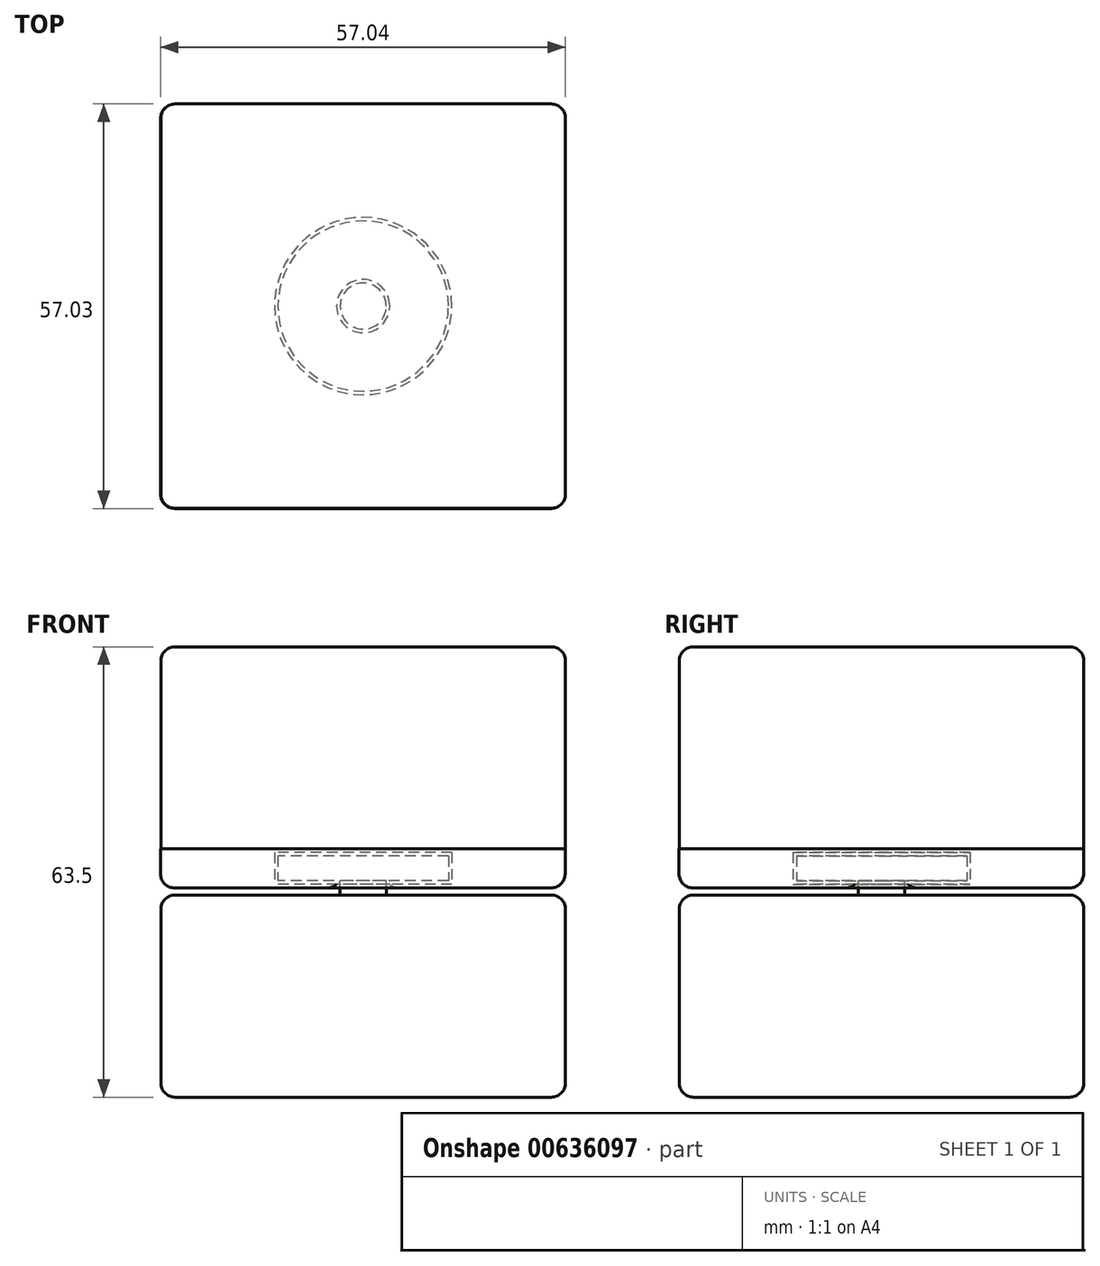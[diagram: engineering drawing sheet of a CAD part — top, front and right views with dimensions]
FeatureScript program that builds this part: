
annotation { "Feature Type Name" : "Feature", "Feature Type Description" : "" }
export const myFeature = defineFeature(function(context is Context, id is Id, definition is map)
    precondition{}
    {
        {
            var Q0;
            Q0=qCreatedBy(makeId("Top.planeOp"),FACE);
            var sketch = newSketch(context, id + "F0", { "sketchPlane" : qUnion([Q0])});
            skCircle(sketch, "E0", {"center": v(0, 0) * mm, "radius": 12.5 * mm});
            skCircle(sketch, "E1", {"center": v(0, 0) * mm, "radius": 13.5 * mm});
            skSolve(sketch);
        }
        {
            var Q0;
            Q0=makeQuery(id+"F0.imprint","IMPRINT",FACE,{"disambiguationData":[TD([[makeQuery(id+"F0.imprint","IMPRINT",EDGE,{"derivedFrom":sQuery(id+"F0.wireOp",EDGE,"E0")}),-1.0]])]});
            extrude(context, id + "F1", {"entities" : qUnion([Q0]), "depth" : 5 * mm, "offsetDistance" : 25 * mm});
        }
        {
            var Q0;
            Q0=qCreatedBy(makeId("Top.planeOp"),FACE);
            cPlane(context, id + "F2", {"entities" : qUnion([Q0]), "cplaneType" : CPlaneType.OFFSET, "offset" : 1 * mm, "width" : 150 * mm, "height" : 150 * mm});
        }
        {
            var Q0;
            Q0=qCreatedBy(id+"F2.planeOp",FACE);
            var sketch = newSketch(context, id + "F3", { "sketchPlane" : qUnion([Q0])});
            skCircle(sketch, "E2", {"center": v(0, 0) * mm, "radius": 12 * mm});
            skSolve(sketch);
        }
        {
            var Q0;
            Q0=makeQuery(id+"F3.imprint","IMPRINT",FACE,{"disambiguationData":[TD([[makeQuery(id+"F3.imprint","IMPRINT",EDGE,{"derivedFrom":sQuery(id+"F3.wireOp",EDGE,"E2")}),1.0]])]});
            extrude(context, id + "F4", {"entities" : qUnion([Q0]), "depth" : 3.5 * mm, "offsetDistance" : 25 * mm});
        }
        {
            var Q0;
            Q0=qCreatedBy(makeId("Top.planeOp"),FACE);
            var sketch = newSketch(context, id + "F5", { "sketchPlane" : qUnion([Q0])});
            skCircle(sketch, "E3", {"center": v(0, 0) * mm, "radius": 12.5 * mm});
            skCircle(sketch, "E4", {"center": v(0, 0) * mm, "radius": 3.75 * mm});
            skSolve(sketch);
        }
        {
            var Q0;
            Q0=makeQuery(id+"F5.imprint","IMPRINT",FACE,{"disambiguationData":[TD([[makeQuery(id+"F5.imprint","IMPRINT",EDGE,{"derivedFrom":sQuery(id+"F5.wireOp",EDGE,"E3")}),1.0]])]});
            extrude(context, id + "F6", {"entities" : qUnion([Q0]), "operationType" : NewBodyOperationType.ADD, "depth" : 0.5 * mm, "offsetDistance" : 25 * mm});
        }
        {
            var Q0;
            Q0=qCreatedBy(makeId("Top.planeOp"),FACE);
            cPlane(context, id + "F7", {"entities" : qUnion([Q0]), "cplaneType" : CPlaneType.OFFSET, "offset" : 5 * mm, "width" : 150 * mm, "height" : 150 * mm});
        }
        {
            var Q0;
            Q0=qCreatedBy(id+"F7.planeOp",FACE);
            var sketch = newSketch(context, id + "F8", { "sketchPlane" : qUnion([Q0])});
            skCircle(sketch, "E5", {"center": v(0, 0) * mm, "radius": 13.5 * mm});
            skSolve(sketch);
        }
        {
            var Q0;
            Q0=makeQuery(id+"F8.imprint","IMPRINT",FACE,{"disambiguationData":[TD([[makeQuery(id+"F8.imprint","IMPRINT",EDGE,{"derivedFrom":sQuery(id+"F8.wireOp",EDGE,"E5")}),1.0]])]});
            extrude(context, id + "F9", {"entities" : qUnion([Q0]), "operationType" : NewBodyOperationType.ADD, "depth" : 0.5 * mm, "offsetDistance" : 25 * mm});
        }
        {
            var Q0;
            Q0=qCreatedBy(id+"F2.planeOp",FACE);
            var sketch = newSketch(context, id + "F10", { "sketchPlane" : qUnion([Q0])});
            skCircle(sketch, "E6", {"center": v(0, 0) * mm, "radius": 3.25 * mm});
            skSolve(sketch);
        }
        {
            var Q0;
            Q0=makeQuery(id+"F10.imprint","IMPRINT",FACE,{"disambiguationData":[TD([[makeQuery(id+"F10.imprint","IMPRINT",EDGE,{"derivedFrom":sQuery(id+"F10.wireOp",EDGE,"E6")}),1.0]])]});
            extrude(context, id + "F11", {"entities" : qUnion([Q0]), "operationType" : NewBodyOperationType.ADD, "depth" : -2 * mm, "offsetDistance" : 25 * mm});
        }
        {
            var Q0;
            Q0=qCreatedBy(makeId("Top.planeOp"),FACE);
            cPlane(context, id + "F12", {"entities" : qUnion([Q0]), "cplaneType" : CPlaneType.OFFSET, "offset" : 1 * mm, "oppositeDirection" : true, "width" : 150 * mm, "height" : 150 * mm});
        }
        {
            var Q0;
            Q0=qCreatedBy(id+"F12.planeOp",FACE);
            var sketch = newSketch(context, id + "F13", { "sketchPlane" : qUnion([Q0])});
            skLineSegment(sketch, "E7.bottom", {"start": v(-28.5, -28.5) * mm, "end": v(28.5, -28.5) * mm});
            skLineSegment(sketch, "E7.top", {"start": v(-28.5, 28.5) * mm, "end": v(28.5, 28.5) * mm});
            skLineSegment(sketch, "E7.left", {"start": v(-28.5, -28.5) * mm, "end": v(-28.5, 28.5) * mm});
            skLineSegment(sketch, "E7.right", {"start": v(28.5, -28.5) * mm, "end": v(28.5, 28.5) * mm});
            skSolve(sketch);
        }
        {
            var Q0;
            Q0=makeQuery(id+"F13.imprint","IMPRINT",FACE,{"disambiguationData":[TD([[makeQuery(id+"F13.imprint","IMPRINT",EDGE,{"derivedFrom":sQuery(id+"F13.wireOp",EDGE,"E7.bottom")}),1.0]])]});
            extrude(context, id + "F14", {"entities" : qUnion([Q0]), "operationType" : NewBodyOperationType.ADD, "depth" : -28.5 * mm, "offsetDistance" : 25 * mm});
        }
        {
            var Q0;
            Q0=makeQuery(id+"F14.opExtrude","CAP_EDGE",EDGE,{"disambiguationData":[OSD([sQuery(id+"F13.wireOp",EDGE,"E7.right")])],"isStart":true});
            var Q1;
            Q1=makeQuery(id+"F14.opExtrude","CAP_EDGE",EDGE,{"disambiguationData":[OSD([sQuery(id+"F13.wireOp",EDGE,"E7.left")])],"isStart":true});
            var Q2;
            Q2=makeQuery(id+"F14.opExtrude","CAP_EDGE",EDGE,{"disambiguationData":[OSD([sQuery(id+"F13.wireOp",EDGE,"E7.bottom")])],"isStart":true});
            var Q3;
            Q3=makeQuery(id+"F14.opExtrude","CAP_EDGE",EDGE,{"disambiguationData":[OSD([sQuery(id+"F13.wireOp",EDGE,"E7.top")])],"isStart":true});
            var Q4;
            Q4=makeQuery(id+"F14.opExtrude","SWEPT_EDGE",EDGE,{"disambiguationData":[OSD([sQuery(id+"F13.wireOp",EDGE,"E7.top"),sQuery(id+"F13.wireOp",EDGE,"E7.left")])]});
            var Q5;
            Q5=makeQuery(id+"F14.opExtrude","SWEPT_EDGE",EDGE,{"disambiguationData":[OSD([sQuery(id+"F13.wireOp",EDGE,"E7.top"),sQuery(id+"F13.wireOp",EDGE,"E7.right")])]});
            var Q6;
            Q6=makeQuery(id+"F14.opExtrude","SWEPT_EDGE",EDGE,{"disambiguationData":[OSD([sQuery(id+"F13.wireOp",EDGE,"E7.bottom"),sQuery(id+"F13.wireOp",EDGE,"E7.left")])]});
            var Q7;
            Q7=makeQuery(id+"F14.opExtrude","SWEPT_EDGE",EDGE,{"disambiguationData":[OSD([sQuery(id+"F13.wireOp",EDGE,"E7.bottom"),sQuery(id+"F13.wireOp",EDGE,"E7.right")])]});
            var Q8;
            Q8=makeQuery(id+"F14.opExtrude","CAP_FACE",FACE,{"disambiguationData":[OSD([sQuery(id+"F13.wireOp",EDGE,"E7.bottom"),sQuery(id+"F13.wireOp",EDGE,"E7.top"),sQuery(id+"F13.wireOp",EDGE,"E7.left"),sQuery(id+"F13.wireOp",EDGE,"E7.right")])],"isStart":false});
            fillet(context, id + "F15", {"entities" : qUnion([Q0, Q1, Q2, Q3, Q4, Q5, Q6, Q7, Q8]), "radius" : 2 * mm, "tangentPropagation" : true, "allowEdgeOverflow" : false});
        }
        {
            var Q0;
            Q0=qCreatedBy(id+"F7.planeOp",FACE);
            cPlane(context, id + "F16", {"entities" : qUnion([Q0]), "cplaneType" : CPlaneType.OFFSET, "offset" : 0.5 * mm, "width" : 150 * mm, "height" : 150 * mm});
        }
        {
            var Q0;
            Q0=qCreatedBy(id+"F16.planeOp",FACE);
            var sketch = newSketch(context, id + "F17", { "sketchPlane" : qUnion([Q0])});
            skLineSegment(sketch, "E8.bottom", {"start": v(-28.5, 28.5) * mm, "end": v(28.5, 28.5) * mm});
            skLineSegment(sketch, "E8.top", {"start": v(-28.5, -28.5) * mm, "end": v(28.5, -28.5) * mm});
            skLineSegment(sketch, "E8.left", {"start": v(-28.5, 28.5) * mm, "end": v(-28.5, -28.5) * mm});
            skLineSegment(sketch, "E8.right", {"start": v(28.5, 28.5) * mm, "end": v(28.5, -28.5) * mm});
            skSolve(sketch);
        }
        {
            var Q0;
            Q0=makeQuery(id+"F17.imprint","IMPRINT",FACE,{"disambiguationData":[TD([[makeQuery(id+"F17.imprint","IMPRINT",EDGE,{"derivedFrom":sQuery(id+"F17.wireOp",EDGE,"E8.bottom")}),-1.0]])]});
            extrude(context, id + "F18", {"entities" : qUnion([Q0]), "operationType" : NewBodyOperationType.ADD, "depth" : 28.5 * mm, "offsetDistance" : 25 * mm});
        }
        {
            var Q0;
            Q0=qCreatedBy(id+"F16.planeOp",FACE);
            var sketch = newSketch(context, id + "F19", { "sketchPlane" : qUnion([Q0])});
            skLineSegment(sketch, "E9.bottom", {"start": v(-28.54, -28.53) * mm, "end": v(28.46, -28.53) * mm});
            skLineSegment(sketch, "E9.top", {"start": v(-28.54, 28.47) * mm, "end": v(28.46, 28.47) * mm});
            skLineSegment(sketch, "E9.left", {"start": v(-28.54, -28.53) * mm, "end": v(-28.54, 28.47) * mm});
            skLineSegment(sketch, "E9.right", {"start": v(28.46, -28.53) * mm, "end": v(28.46, 28.47) * mm});
            skCircle(sketch, "E10", {"center": v(0, 0) * mm, "radius": 13.5 * mm});
            skSolve(sketch);
        }
        {
            var Q0;
            Q0=makeQuery(id+"F19.imprint","IMPRINT",FACE,{"disambiguationData":[TD([[makeQuery(id+"F19.imprint","IMPRINT",EDGE,{"derivedFrom":sQuery(id+"F19.wireOp",EDGE,"E9.bottom")}),1.0]])]});
            extrude(context, id + "F20", {"entities" : qUnion([Q0]), "operationType" : NewBodyOperationType.ADD, "oppositeDirection" : true, "depth" : 5.5 * mm, "offsetDistance" : 25 * mm});
        }
        {
            var Q0;
            Q0=makeQuery(id+"F18.opExtrude","SWEPT_EDGE",EDGE,{"disambiguationData":[OSD([sQuery(id+"F17.wireOp",EDGE,"E8.bottom"),sQuery(id+"F17.wireOp",EDGE,"E8.right")])]});
            var Q1;
            Q1=makeQuery(id+"F20.opExtrude","SWEPT_EDGE",EDGE,{"disambiguationData":[OSD([sQuery(id+"F19.wireOp",EDGE,"E9.top"),sQuery(id+"F19.wireOp",EDGE,"E9.right")])]});
            var Q2;
            Q2=makeQuery(id+"F18.opExtrude","CAP_FACE",FACE,{"disambiguationData":[OSD([sQuery(id+"F17.wireOp",EDGE,"E8.bottom"),sQuery(id+"F17.wireOp",EDGE,"E8.top"),sQuery(id+"F17.wireOp",EDGE,"E8.left"),sQuery(id+"F17.wireOp",EDGE,"E8.right")])],"isStart":false});
            var Q3;
            Q3=makeQuery(id+"F18.opExtrude","SWEPT_EDGE",EDGE,{"disambiguationData":[OSD([sQuery(id+"F17.wireOp",EDGE,"E8.top"),sQuery(id+"F17.wireOp",EDGE,"E8.right")])]});
            var Q4;
            Q4=makeQuery(id+"F18.opExtrude","SWEPT_EDGE",EDGE,{"disambiguationData":[OSD([sQuery(id+"F17.wireOp",EDGE,"E8.top"),sQuery(id+"F17.wireOp",EDGE,"E8.left")])]});
            var Q5;
            Q5=makeQuery(id+"F18.opExtrude","SWEPT_EDGE",EDGE,{"disambiguationData":[OSD([sQuery(id+"F17.wireOp",EDGE,"E8.bottom"),sQuery(id+"F17.wireOp",EDGE,"E8.left")])]});
            fillet(context, id + "F21", {"entities" : qUnion([Q0, Q1, Q2, Q3, Q4, Q5]), "radius" : 2 * mm, "tangentPropagation" : true, "allowEdgeOverflow" : false});
        }
        {
            var Q0;
            Q0=makeQuery(id+"F20.opExtrude","SWEPT_EDGE",EDGE,{"disambiguationData":[OSD([sQuery(id+"F19.wireOp",EDGE,"E9.bottom"),sQuery(id+"F19.wireOp",EDGE,"E9.right")])]});
            var Q1;
            Q1=makeQuery(id+"F20.opExtrude","SWEPT_EDGE",EDGE,{"disambiguationData":[OSD([sQuery(id+"F19.wireOp",EDGE,"E9.bottom"),sQuery(id+"F19.wireOp",EDGE,"E9.left")])]});
            var Q2;
            Q2=makeQuery(id+"F20.opExtrude","SWEPT_EDGE",EDGE,{"disambiguationData":[OSD([sQuery(id+"F19.wireOp",EDGE,"E9.top"),sQuery(id+"F19.wireOp",EDGE,"E9.left")])]});
            var Q3;
            Q3=makeQuery(id+"F20.boolean.opBoolean","MERGE",FACE,{"derivedFrom":[makeQuery(id+"F6.boolean.opBoolean","MERGE",FACE,{"derivedFrom":[makeQuery(id+"F1.opExtrude","CAP_FACE",FACE,{"disambiguationData":[OSD([sQuery(id+"F0.wireOp",EDGE,"E0"),sQuery(id+"F0.wireOp",EDGE,"E1")])],"isStart":true}),makeQuery(id+"F6.opExtrude","CAP_FACE",FACE,{"disambiguationData":[OSD([sQuery(id+"F5.wireOp",EDGE,"E3"),sQuery(id+"F5.wireOp",EDGE,"E4")])],"isStart":true})]}),makeQuery(id+"F20.opExtrude","CAP_FACE",FACE,{"disambiguationData":[OSD([sQuery(id+"F19.wireOp",EDGE,"E9.bottom"),sQuery(id+"F19.wireOp",EDGE,"E9.top"),sQuery(id+"F19.wireOp",EDGE,"E9.left"),sQuery(id+"F19.wireOp",EDGE,"E9.right"),sQuery(id+"F19.wireOp",EDGE,"E10")])],"isStart":false})]});
            var Q4;
            Q4=makeQuery(id+"F6.opExtrude","CAP_EDGE",EDGE,{"disambiguationData":[OSD([sQuery(id+"F5.wireOp",EDGE,"E4")])],"isStart":true});
            fillet(context, id + "F22", {"entities" : qUnion([Q0, Q1, Q2, Q3, Q4]), "radius" : 2 * mm, "tangentPropagation" : true, "allowEdgeOverflow" : false});
        }
    });
